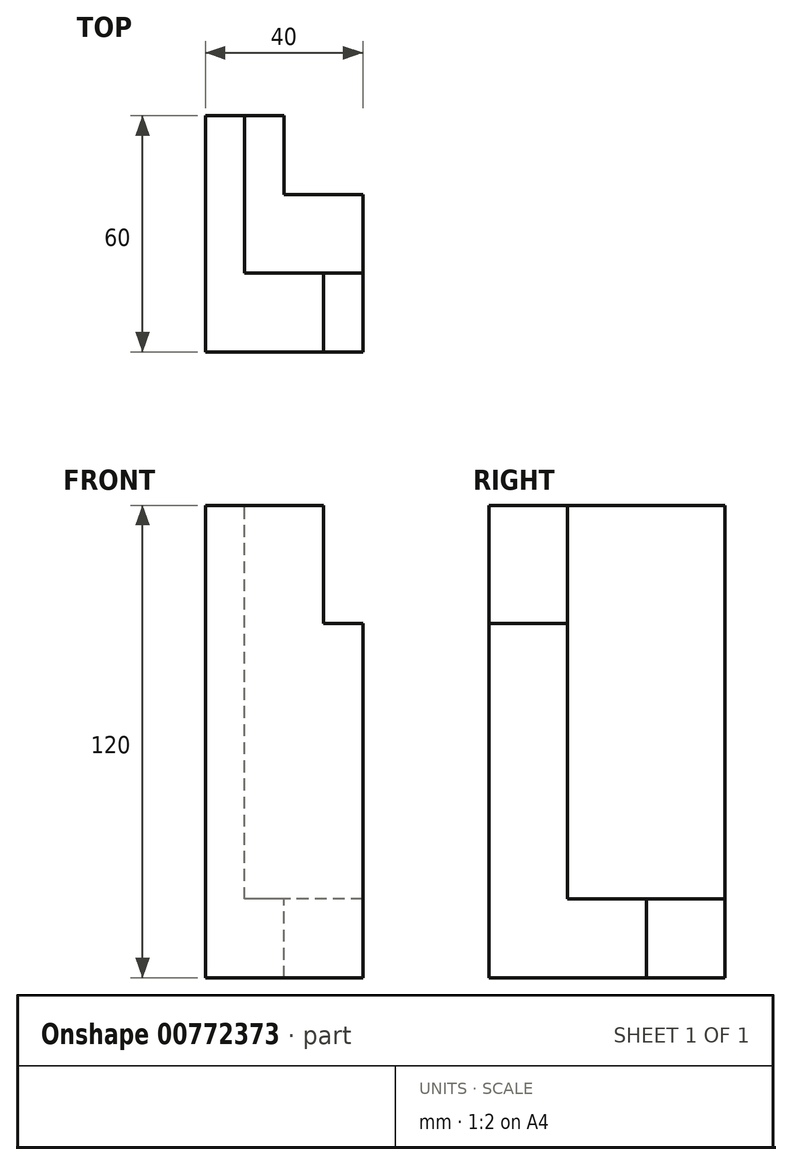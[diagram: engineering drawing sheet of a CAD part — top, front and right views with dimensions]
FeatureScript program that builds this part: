
annotation { "Feature Type Name" : "Feature", "Feature Type Description" : "" }
export const myFeature = defineFeature(function(context is Context, id is Id, definition is map)
    precondition{}
    {
        {
            var Q0;
            Q0=qCreatedBy(makeId("Top.planeOp"),FACE);
            var sketch = newSketch(context, id + "F0", { "sketchPlane" : qUnion([Q0])});
            skLineSegment(sketch, "E0", {"start": v(0, 0) * mm, "end": v(40, 0) * mm});
            skLineSegment(sketch, "E1", {"start": v(40, 0) * mm, "end": v(40, 40) * mm});
            skLineSegment(sketch, "E2", {"start": v(40, 40) * mm, "end": v(20, 40) * mm});
            skLineSegment(sketch, "E3", {"start": v(20, 40) * mm, "end": v(20, 60) * mm});
            skLineSegment(sketch, "E4", {"start": v(20, 60) * mm, "end": v(0, 60) * mm});
            skLineSegment(sketch, "E5", {"start": v(0, 60) * mm, "end": v(0, 0) * mm});
            skLineSegment(sketch, "E6", {"start": v(40, 20) * mm, "end": v(0, 20) * mm});
            skLineSegment(sketch, "E7", {"start": v(30, 20) * mm, "end": v(30, 0) * mm});
            skPoint(sketch, "E7.endSnap0", {"position": v(20, 0) * mm});
            skLineSegment(sketch, "E8", {"start": v(10, 60) * mm, "end": v(10, 20) * mm});
            skSolve(sketch);
        }
        {
            var Q0;
            {var subQ3=sQuery(id+"F0.wireOp",EDGE,"E8");Q0=makeQuery(id+"F0.imprint","IMPRINT",FACE,{"disambiguationData":[TD([[makeQuery(id+"F0.imprint","IMPRINT",EDGE,{"derivedFrom":subQ3}),-1.0]])]});}
            var Q1;
            {var subQ3=sQuery(id+"F0.wireOp",EDGE,"E2");Q1=makeQuery(id+"F0.imprint","IMPRINT",FACE,{"disambiguationData":[TD([[makeQuery(id+"F0.imprint","IMPRINT",EDGE,{"derivedFrom":subQ3}),1.0]])]});}
            var Q2;
            {var subQ3=sQuery(id+"F0.wireOp",EDGE,"E7");Q2=makeQuery(id+"F0.imprint","IMPRINT",FACE,{"disambiguationData":[TD([[makeQuery(id+"F0.imprint","IMPRINT",EDGE,{"derivedFrom":subQ3}),1.0]])]});}
            var Q3;
            {var subQ4=sQuery(id+"F0.wireOp",EDGE,"E7");Q3=makeQuery(id+"F0.imprint","IMPRINT",FACE,{"disambiguationData":[TD([[makeQuery(id+"F0.imprint","IMPRINT",EDGE,{"derivedFrom":subQ4}),-1.0]])]});}
            extrude(context, id + "F1", {"entities" : qUnion([Q0, Q1, Q2, Q3]), "oppositeDirection" : true, "depth" : 120 * mm, "offsetDistance" : 25 * mm});
        }
        {
            var Q0;
            {var subQ3=sQuery(id+"F0.wireOp",EDGE,"E7");Q0=makeQuery(id+"F0.imprint","IMPRINT",FACE,{"disambiguationData":[TD([[makeQuery(id+"F0.imprint","IMPRINT",EDGE,{"derivedFrom":subQ3}),1.0]])]});}
            var Q1;
            {var subQ3=sQuery(id+"F0.wireOp",EDGE,"E2");Q1=makeQuery(id+"F0.imprint","IMPRINT",FACE,{"disambiguationData":[TD([[makeQuery(id+"F0.imprint","IMPRINT",EDGE,{"derivedFrom":subQ3}),1.0]])]});}
            extrude(context, id + "F2", {"entities" : qUnion([Q0, Q1]), "operationType" : NewBodyOperationType.REMOVE, "oppositeDirection" : true, "depth" : 30 * mm, "offsetDistance" : 25 * mm});
        }
        {
            var Q0;
            {var subQ3=sQuery(id+"F0.wireOp",EDGE,"E2");Q0=makeQuery(id+"F0.imprint","IMPRINT",FACE,{"disambiguationData":[TD([[makeQuery(id+"F0.imprint","IMPRINT",EDGE,{"derivedFrom":subQ3}),1.0]])]});}
            extrude(context, id + "F3", {"entities" : qUnion([Q0]), "operationType" : NewBodyOperationType.REMOVE, "oppositeDirection" : true, "depth" : 100 * mm, "offsetDistance" : 25 * mm});
        }
    });
